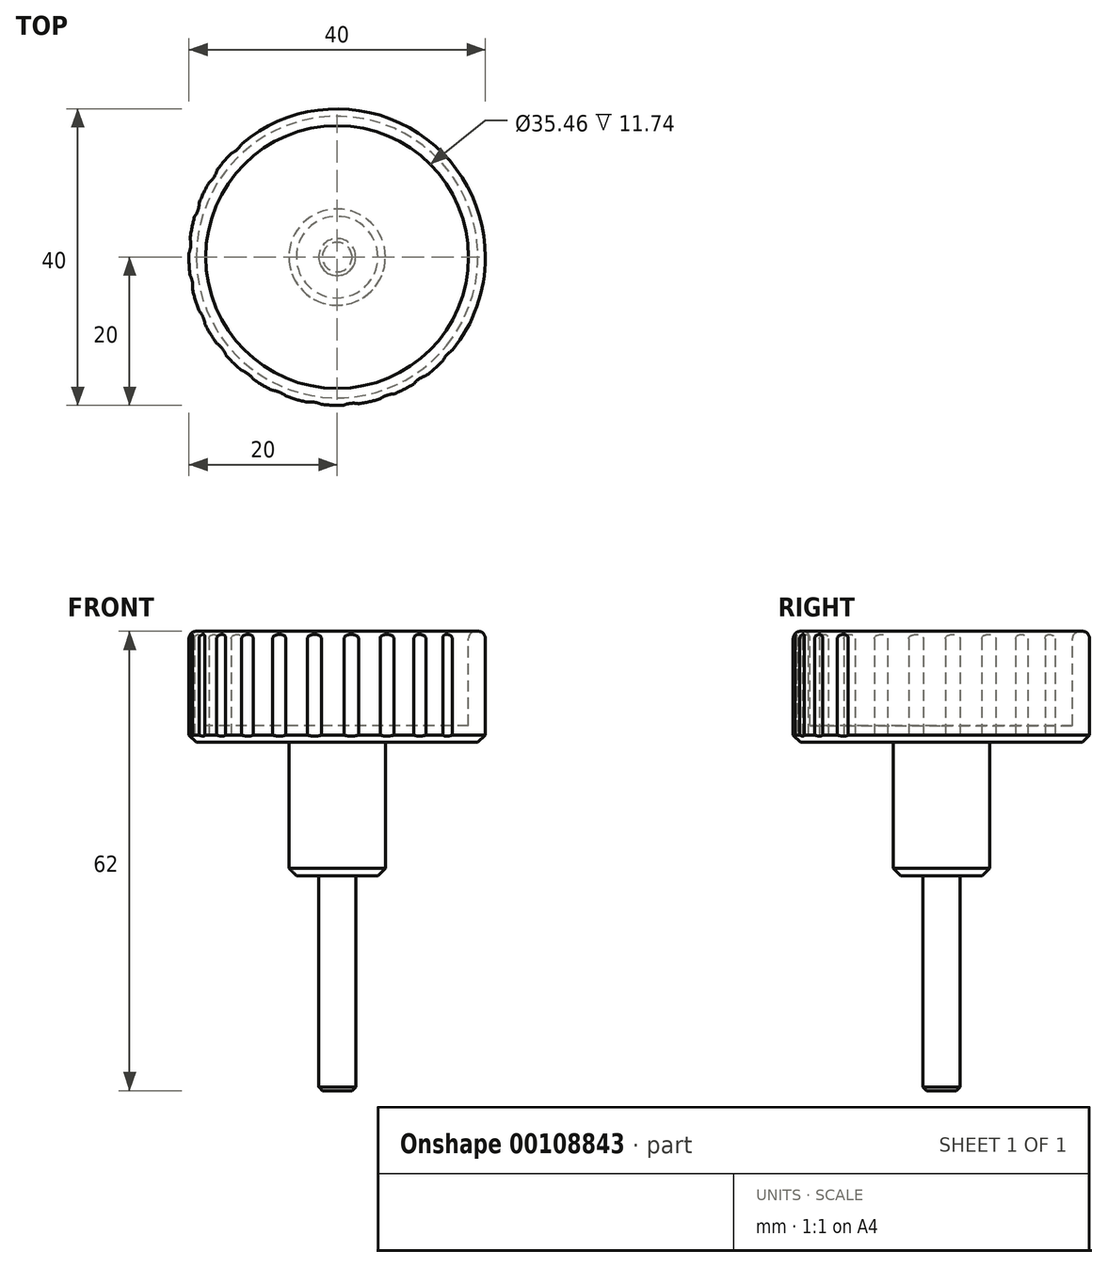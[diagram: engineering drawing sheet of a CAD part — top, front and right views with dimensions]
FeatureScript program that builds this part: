
annotation { "Feature Type Name" : "Feature", "Feature Type Description" : "" }
export const myFeature = defineFeature(function(context is Context, id is Id, definition is map)
    precondition{}
    {
        {
            var Q0;
            Q0=qCreatedBy(makeId("Front.planeOp"),FACE);
            var sketch = newSketch(context, id + "F0", { "sketchPlane" : qUnion([Q0])});
            skLineSegment(sketch, "E0", {"start": v(0, 56.29) * mm, "end": v(0, 50.52) * mm, "construction": true});
            skLineSegment(sketch, "E1", {"start": v(-48.57, 0) * mm, "end": v(48.76, 0) * mm, "construction": true});
            skLineSegment(sketch, "E2", {"start": v(-27.43, 50.52) * mm, "end": v(-17.73, 50.52) * mm, "construction": true});
            skLineSegment(sketch, "E3", {"start": v(-25.14, 35.52) * mm, "end": v(28.57, 35.52) * mm, "construction": true});
            skLineSegment(sketch, "E4", {"start": v(-11.83, 17.52) * mm, "end": v(17.7, 17.52) * mm, "construction": true});
            skLineSegment(sketch, "E5", {"start": v(-5.55, -11.48) * mm, "end": v(12.36, -11.48) * mm, "construction": true});
            skLineSegment(sketch, "E6", {"start": v(-17.73, 50.52) * mm, "end": v(-20, 50.52) * mm});
            skLineSegment(sketch, "E7", {"start": v(-20, 50.52) * mm, "end": v(-20, 35.52) * mm});
            skLineSegment(sketch, "E8", {"start": v(-20, 35.52) * mm, "end": v(-6.5, 35.52) * mm});
            skLineSegment(sketch, "E9", {"start": v(-6.5, 35.52) * mm, "end": v(-6.5, 17.52) * mm});
            skLineSegment(sketch, "E10", {"start": v(-6.5, 17.52) * mm, "end": v(-2.5, 17.52) * mm});
            skLineSegment(sketch, "E11", {"start": v(-2.5, 17.52) * mm, "end": v(-2.5, -11.48) * mm});
            skLineSegment(sketch, "E12", {"start": v(-2.5, -11.48) * mm, "end": v(0, -11.48) * mm});
            skLineSegment(sketch, "E13", {"start": v(0, -11.48) * mm, "end": v(0, 37.78) * mm});
            skLineSegment(sketch, "E14", {"start": v(-2.5, 17.52) * mm, "end": v(0, 17.52) * mm});
            skLineSegment(sketch, "E15", {"start": v(-17.73, 50.52) * mm, "end": v(-17.73, 37.78) * mm});
            skLineSegment(sketch, "E16", {"start": v(-17.73, 37.78) * mm, "end": v(0, 37.78) * mm});
            skLineSegment(sketch, "E17.trimOffspring", {"start": v(0, 50.52) * mm, "end": v(34.67, 50.52) * mm, "construction": true});
            skLineSegment(sketch, "E18.trimOffspring", {"start": v(0, 37.78) * mm, "end": v(0, -52.48) * mm, "construction": true});
            skSolve(sketch);
        }
        {
            var Q0;
            Q0=makeQuery(id+"F0.imprint","IMPRINT",FACE,{"disambiguationData":[TD([[makeQuery(id+"F0.imprint","IMPRINT",EDGE,{"derivedFrom":sQuery(id+"F0.wireOp",EDGE,"E11")}),1.0]])]});
            var Q1;
            Q1=sQuery(id+"F0.wireOp",EDGE,"E0");
            revolve(context, id + "F1", {"entities" : qUnion([Q0]), "axis" : qUnion([Q1]), "revolveType" : RevolveType.FULL});
        }
        {
            var Q0;
            Q0 = qSketchRegion(id + "F0", true);
            var Q1;
            Q1=sQuery(id+"F0.wireOp",EDGE,"E0");
            revolve(context, id + "F2", {"operationType" : NewBodyOperationType.ADD, "entities" : qUnion([Q0]), "axis" : qUnion([Q1]), "revolveType" : RevolveType.FULL});
        }
        {
            var Q0;
            Q0=makeQuery(id+"F2.opRevolve","SWEPT_EDGE",EDGE,{"disambiguationData":[OSD([sQuery(id+"F0.wireOp",EDGE,"E9"),sQuery(id+"F0.wireOp",EDGE,"E10")])]});
            var Q1;
            Q1=makeQuery(id+"F2.opRevolve","SWEPT_EDGE",EDGE,{"disambiguationData":[OSD([sQuery(id+"F0.wireOp",EDGE,"E7"),sQuery(id+"F0.wireOp",EDGE,"E8")])]});
            chamfer(context, id + "F3", {"entities" : qUnion([Q0, Q1]), "width" : 1 * mm, "tangentPropagation" : true});
        }
        {
            var Q0;
            Q0=makeQuery(id+"F1.opRevolve","SWEPT_EDGE",EDGE,{"disambiguationData":[OSD([sQuery(id+"F0.wireOp",EDGE,"E11"),sQuery(id+"F0.wireOp",EDGE,"E12")])]});
            chamfer(context, id + "F4", {"entities" : qUnion([Q0]), "width" : 0.5 * mm, "tangentPropagation" : true});
        }
        {
            var Q0;
            Q0=makeQuery(id+"F2.opRevolve","SWEPT_EDGE",EDGE,{"disambiguationData":[OSD([sQuery(id+"F0.wireOp",EDGE,"E6"),sQuery(id+"F0.wireOp",EDGE,"E7")])]});
            var Q1;
            Q1=makeQuery(id+"F2.opRevolve","SWEPT_EDGE",EDGE,{"disambiguationData":[OSD([sQuery(id+"F0.wireOp",EDGE,"E6"),sQuery(id+"F0.wireOp",EDGE,"E15")])]});
            fillet(context, id + "F5", {"entities" : qUnion([Q0, Q1]), "radius" : 1 * mm, "tangentPropagation" : true, "allowEdgeOverflow" : false});
        }
        {
            var Q0;
            Q0=makeQuery(id+"F2.opRevolve","SWEPT_FACE",FACE,{"disambiguationData":[OSD([sQuery(id+"F0.wireOp",EDGE,"E8")])]});
            cPlane(context, id + "F6", {"entities" : qUnion([Q0]), "cplaneType" : CPlaneType.OFFSET, "offset" : 0 * mm, "width" : 150 * mm, "height" : 150 * mm});
        }
        {
            var Q0;
            Q0=qCreatedBy(id+"F6.planeOp",FACE);
            var sketch = newSketch(context, id + "F7", { "sketchPlane" : qUnion([Q0])});
            skCircle(sketch, "E19", {"center": v(0, -23.03) * mm, "radius": 3.2 * mm});
            skCircle(sketch, "E20", {"center": v(0, 0) * mm, "radius": 23.02 * mm, "construction": true});
            skCircle(sketch, "E21.1.0", {"center": v(-5.67, -22.32) * mm, "radius": 3.2 * mm});
            skCircle(sketch, "E21.2.0", {"center": v(-11, -20.23) * mm, "radius": 3.2 * mm});
            skCircle(sketch, "E21.3.0", {"center": v(-15.65, -16.9) * mm, "radius": 3.2 * mm});
            skCircle(sketch, "E21.4.0", {"center": v(-19.33, -12.52) * mm, "radius": 3.2 * mm});
            skCircle(sketch, "E21.5.0", {"center": v(-21.82, -7.37) * mm, "radius": 3.2 * mm});
            skCircle(sketch, "E21.6.0", {"center": v(-22.96, -1.77) * mm, "radius": 3.2 * mm});
            skCircle(sketch, "E21.7.0", {"center": v(-22.69, 3.94) * mm, "radius": 3.2 * mm});
            skCircle(sketch, "E21.8.0", {"center": v(-21.02, 9.41) * mm, "radius": 3.2 * mm});
            skCircle(sketch, "E21.9.0", {"center": v(-18.05, 14.3) * mm, "radius": 3.2 * mm});
            skCircle(sketch, "E21.10.0", {"center": v(-13.97, 18.3) * mm, "radius": 3.2 * mm});
            skCircle(sketch, "E21.11.0", {"center": v(-9.03, 21.18) * mm, "radius": 3.2 * mm});
            skCircle(sketch, "E21.12.0", {"center": v(-3.53, 22.76) * mm, "radius": 3.2 * mm});
            skCircle(sketch, "E21.13.0", {"center": v(2.19, 22.92) * mm, "radius": 3.2 * mm});
            skCircle(sketch, "E21.14.0", {"center": v(7.77, 21.68) * mm, "radius": 3.2 * mm});
            skCircle(sketch, "E21.15.0", {"center": v(12.87, 19.1) * mm, "radius": 3.2 * mm});
            skCircle(sketch, "E21.16.0", {"center": v(17.18, 15.34) * mm, "radius": 3.2 * mm});
            skCircle(sketch, "E21.17.0", {"center": v(20.43, 10.63) * mm, "radius": 3.2 * mm});
            skCircle(sketch, "E21.18.0", {"center": v(22.42, 5.27) * mm, "radius": 3.2 * mm});
            skCircle(sketch, "E21.19.0", {"center": v(23.02, -0.42) * mm, "radius": 3.2 * mm});
            skCircle(sketch, "E21.20.0", {"center": v(22.21, -6.08) * mm, "radius": 3.2 * mm});
            skCircle(sketch, "E21.21.0", {"center": v(20.03, -11.36) * mm, "radius": 3.2 * mm});
            skCircle(sketch, "E21.22.0", {"center": v(16.61, -15.95) * mm, "radius": 3.2 * mm});
            skCircle(sketch, "E21.23.0", {"center": v(12.17, -19.55) * mm, "radius": 3.2 * mm});
            skCircle(sketch, "E21.24.0", {"center": v(6.98, -21.95) * mm, "radius": 3.2 * mm});
            skLineSegment(sketch, "E21.anchor1", {"start": v(0, 0) * mm, "end": v(0, -23.03) * mm, "construction": true});
            skLineSegment(sketch, "E21.anchor2", {"start": v(0, 0) * mm, "end": v(6.98, -21.95) * mm, "construction": true});
            skSolve(sketch);
        }
        {
            var Q0;
            {var subQ0=sQuery(id+"F7.wireOp",EDGE,"E21.2.0");var subQ1=sQuery(id+"F7.wireOp",EDGE,"E21.1.0");var subQ2=makeQuery(id+"F7.imprint","INTERSECT",VERTEX,{"disambiguationData":[OD(0.0)],"derivedFrom":[subQ1,subQ0]});Q0=makeQuery(id+"F7.imprint","IMPRINT",FACE,{"disambiguationData":[TD([[makeQuery(id+"F7.imprint","IMPRINT",EDGE,{"disambiguationData":[TD([[subQ2,-1.0]])],"derivedFrom":subQ1}),-1.0]])]});}
            var Q1;
            {var subQ0=sQuery(id+"F7.wireOp",EDGE,"E21.1.0");var subQ1=sQuery(id+"F7.wireOp",EDGE,"E19");var subQ2=makeQuery(id+"F7.imprint","INTERSECT",VERTEX,{"disambiguationData":[OD(0.0)],"derivedFrom":[subQ1,subQ0]});Q1=makeQuery(id+"F7.imprint","IMPRINT",FACE,{"disambiguationData":[TD([[makeQuery(id+"F7.imprint","IMPRINT",EDGE,{"disambiguationData":[TD([[subQ2,-1.0]])],"derivedFrom":subQ1}),-1.0]])]});}
            var Q2;
            {var subQ0=sQuery(id+"F7.wireOp",EDGE,"E21.1.0");var subQ1=sQuery(id+"F7.wireOp",EDGE,"E19");var subQ2=makeQuery(id+"F7.imprint","INTERSECT",VERTEX,{"disambiguationData":[OD(0.0)],"derivedFrom":[subQ1,subQ0]});Q2=makeQuery(id+"F7.imprint","IMPRINT",FACE,{"disambiguationData":[TD([[makeQuery(id+"F7.imprint","IMPRINT",EDGE,{"disambiguationData":[TD([[subQ2,1.0]])],"derivedFrom":subQ1}),1.0]])]});}
            var Q3;
            {var subQ0=sQuery(id+"F7.wireOp",EDGE,"E21.24.0");var subQ1=sQuery(id+"F7.wireOp",EDGE,"E21.23.0");var subQ2=makeQuery(id+"F7.imprint","INTERSECT",VERTEX,{"disambiguationData":[OD(0.0)],"derivedFrom":[subQ1,subQ0]});Q3=makeQuery(id+"F7.imprint","IMPRINT",FACE,{"disambiguationData":[TD([[makeQuery(id+"F7.imprint","IMPRINT",EDGE,{"disambiguationData":[TD([[subQ2,-1.0]])],"derivedFrom":subQ1}),-1.0]])]});}
            var Q4;
            {var subQ0=sQuery(id+"F7.wireOp",EDGE,"E21.23.0");var subQ1=sQuery(id+"F7.wireOp",EDGE,"E21.22.0");var subQ2=makeQuery(id+"F7.imprint","INTERSECT",VERTEX,{"disambiguationData":[OD(0.0)],"derivedFrom":[subQ1,subQ0]});Q4=makeQuery(id+"F7.imprint","IMPRINT",FACE,{"disambiguationData":[TD([[makeQuery(id+"F7.imprint","IMPRINT",EDGE,{"disambiguationData":[TD([[subQ2,-1.0]])],"derivedFrom":subQ1}),-1.0]])]});}
            var Q5;
            {var subQ0=sQuery(id+"F7.wireOp",EDGE,"E21.22.0");var subQ1=sQuery(id+"F7.wireOp",EDGE,"E21.21.0");var subQ2=makeQuery(id+"F7.imprint","INTERSECT",VERTEX,{"disambiguationData":[OD(0.0)],"derivedFrom":[subQ1,subQ0]});Q5=makeQuery(id+"F7.imprint","IMPRINT",FACE,{"disambiguationData":[TD([[makeQuery(id+"F7.imprint","IMPRINT",EDGE,{"disambiguationData":[TD([[subQ2,-1.0]])],"derivedFrom":subQ1}),-1.0]])]});}
            var Q6;
            {var subQ0=sQuery(id+"F7.wireOp",EDGE,"E21.21.0");var subQ1=sQuery(id+"F7.wireOp",EDGE,"E21.20.0");var subQ2=makeQuery(id+"F7.imprint","INTERSECT",VERTEX,{"disambiguationData":[OD(0.0)],"derivedFrom":[subQ1,subQ0]});Q6=makeQuery(id+"F7.imprint","IMPRINT",FACE,{"disambiguationData":[TD([[makeQuery(id+"F7.imprint","IMPRINT",EDGE,{"disambiguationData":[TD([[subQ2,-1.0]])],"derivedFrom":subQ1}),-1.0]])]});}
            var Q7;
            {var subQ0=sQuery(id+"F7.wireOp",EDGE,"E21.20.0");var subQ1=sQuery(id+"F7.wireOp",EDGE,"E21.19.0");var subQ2=makeQuery(id+"F7.imprint","INTERSECT",VERTEX,{"disambiguationData":[OD(0.0)],"derivedFrom":[subQ1,subQ0]});Q7=makeQuery(id+"F7.imprint","IMPRINT",FACE,{"disambiguationData":[TD([[makeQuery(id+"F7.imprint","IMPRINT",EDGE,{"disambiguationData":[TD([[subQ2,-1.0]])],"derivedFrom":subQ1}),-1.0]])]});}
            var Q8;
            {var subQ0=sQuery(id+"F7.wireOp",EDGE,"E21.19.0");var subQ1=sQuery(id+"F7.wireOp",EDGE,"E21.18.0");var subQ2=makeQuery(id+"F7.imprint","INTERSECT",VERTEX,{"disambiguationData":[OD(0.0)],"derivedFrom":[subQ1,subQ0]});Q8=makeQuery(id+"F7.imprint","IMPRINT",FACE,{"disambiguationData":[TD([[makeQuery(id+"F7.imprint","IMPRINT",EDGE,{"disambiguationData":[TD([[subQ2,-1.0]])],"derivedFrom":subQ1}),-1.0]])]});}
            var Q9;
            {var subQ0=sQuery(id+"F7.wireOp",EDGE,"E21.18.0");var subQ1=sQuery(id+"F7.wireOp",EDGE,"E21.17.0");var subQ2=makeQuery(id+"F7.imprint","INTERSECT",VERTEX,{"disambiguationData":[OD(0.0)],"derivedFrom":[subQ1,subQ0]});Q9=makeQuery(id+"F7.imprint","IMPRINT",FACE,{"disambiguationData":[TD([[makeQuery(id+"F7.imprint","IMPRINT",EDGE,{"disambiguationData":[TD([[subQ2,-1.0]])],"derivedFrom":subQ1}),-1.0]])]});}
            var Q10;
            {var subQ0=sQuery(id+"F7.wireOp",EDGE,"E21.17.0");var subQ1=sQuery(id+"F7.wireOp",EDGE,"E21.16.0");var subQ2=makeQuery(id+"F7.imprint","INTERSECT",VERTEX,{"disambiguationData":[OD(0.0)],"derivedFrom":[subQ1,subQ0]});Q10=makeQuery(id+"F7.imprint","IMPRINT",FACE,{"disambiguationData":[TD([[makeQuery(id+"F7.imprint","IMPRINT",EDGE,{"disambiguationData":[TD([[subQ2,-1.0]])],"derivedFrom":subQ1}),-1.0]])]});}
            var Q11;
            {var subQ0=sQuery(id+"F7.wireOp",EDGE,"E21.16.0");var subQ1=sQuery(id+"F7.wireOp",EDGE,"E21.15.0");var subQ2=makeQuery(id+"F7.imprint","INTERSECT",VERTEX,{"disambiguationData":[OD(0.0)],"derivedFrom":[subQ1,subQ0]});Q11=makeQuery(id+"F7.imprint","IMPRINT",FACE,{"disambiguationData":[TD([[makeQuery(id+"F7.imprint","IMPRINT",EDGE,{"disambiguationData":[TD([[subQ2,-1.0]])],"derivedFrom":subQ1}),-1.0]])]});}
            var Q12;
            {var subQ0=sQuery(id+"F7.wireOp",EDGE,"E21.15.0");var subQ1=sQuery(id+"F7.wireOp",EDGE,"E21.14.0");var subQ2=makeQuery(id+"F7.imprint","INTERSECT",VERTEX,{"disambiguationData":[OD(0.0)],"derivedFrom":[subQ1,subQ0]});Q12=makeQuery(id+"F7.imprint","IMPRINT",FACE,{"disambiguationData":[TD([[makeQuery(id+"F7.imprint","IMPRINT",EDGE,{"disambiguationData":[TD([[subQ2,-1.0]])],"derivedFrom":subQ1}),-1.0]])]});}
            var Q13;
            {var subQ0=sQuery(id+"F7.wireOp",EDGE,"E21.14.0");var subQ1=sQuery(id+"F7.wireOp",EDGE,"E21.13.0");var subQ2=makeQuery(id+"F7.imprint","INTERSECT",VERTEX,{"disambiguationData":[OD(0.0)],"derivedFrom":[subQ1,subQ0]});Q13=makeQuery(id+"F7.imprint","IMPRINT",FACE,{"disambiguationData":[TD([[makeQuery(id+"F7.imprint","IMPRINT",EDGE,{"disambiguationData":[TD([[subQ2,-1.0]])],"derivedFrom":subQ1}),-1.0]])]});}
            var Q14;
            {var subQ0=sQuery(id+"F7.wireOp",EDGE,"E21.13.0");var subQ1=sQuery(id+"F7.wireOp",EDGE,"E21.12.0");var subQ2=makeQuery(id+"F7.imprint","INTERSECT",VERTEX,{"disambiguationData":[OD(0.0)],"derivedFrom":[subQ1,subQ0]});Q14=makeQuery(id+"F7.imprint","IMPRINT",FACE,{"disambiguationData":[TD([[makeQuery(id+"F7.imprint","IMPRINT",EDGE,{"disambiguationData":[TD([[subQ2,-1.0]])],"derivedFrom":subQ1}),-1.0]])]});}
            var Q15;
            {var subQ0=sQuery(id+"F7.wireOp",EDGE,"E21.12.0");var subQ1=sQuery(id+"F7.wireOp",EDGE,"E21.11.0");var subQ2=makeQuery(id+"F7.imprint","INTERSECT",VERTEX,{"disambiguationData":[OD(0.0)],"derivedFrom":[subQ1,subQ0]});Q15=makeQuery(id+"F7.imprint","IMPRINT",FACE,{"disambiguationData":[TD([[makeQuery(id+"F7.imprint","IMPRINT",EDGE,{"disambiguationData":[TD([[subQ2,-1.0]])],"derivedFrom":subQ1}),-1.0]])]});}
            var Q16;
            {var subQ0=sQuery(id+"F7.wireOp",EDGE,"E21.10.0");var subQ1=sQuery(id+"F7.wireOp",EDGE,"E21.9.0");var subQ2=makeQuery(id+"F7.imprint","INTERSECT",VERTEX,{"disambiguationData":[OD(0.0)],"derivedFrom":[subQ1,subQ0]});Q16=makeQuery(id+"F7.imprint","IMPRINT",FACE,{"disambiguationData":[TD([[makeQuery(id+"F7.imprint","IMPRINT",EDGE,{"disambiguationData":[TD([[subQ2,-1.0]])],"derivedFrom":subQ1}),-1.0]])]});}
            var Q17;
            {var subQ0=sQuery(id+"F7.wireOp",EDGE,"E21.7.0");var subQ1=sQuery(id+"F7.wireOp",EDGE,"E21.6.0");var subQ2=makeQuery(id+"F7.imprint","INTERSECT",VERTEX,{"disambiguationData":[OD(0.0)],"derivedFrom":[subQ1,subQ0]});Q17=makeQuery(id+"F7.imprint","IMPRINT",FACE,{"disambiguationData":[TD([[makeQuery(id+"F7.imprint","IMPRINT",EDGE,{"disambiguationData":[TD([[subQ2,-1.0]])],"derivedFrom":subQ1}),-1.0]])]});}
            var Q18;
            {var subQ0=sQuery(id+"F7.wireOp",EDGE,"E21.6.0");var subQ1=sQuery(id+"F7.wireOp",EDGE,"E21.5.0");var subQ2=makeQuery(id+"F7.imprint","INTERSECT",VERTEX,{"disambiguationData":[OD(0.0)],"derivedFrom":[subQ1,subQ0]});Q18=makeQuery(id+"F7.imprint","IMPRINT",FACE,{"disambiguationData":[TD([[makeQuery(id+"F7.imprint","IMPRINT",EDGE,{"disambiguationData":[TD([[subQ2,-1.0]])],"derivedFrom":subQ1}),-1.0]])]});}
            var Q19;
            {var subQ0=sQuery(id+"F7.wireOp",EDGE,"E21.5.0");var subQ1=sQuery(id+"F7.wireOp",EDGE,"E21.4.0");var subQ2=makeQuery(id+"F7.imprint","INTERSECT",VERTEX,{"disambiguationData":[OD(0.0)],"derivedFrom":[subQ1,subQ0]});Q19=makeQuery(id+"F7.imprint","IMPRINT",FACE,{"disambiguationData":[TD([[makeQuery(id+"F7.imprint","IMPRINT",EDGE,{"disambiguationData":[TD([[subQ2,-1.0]])],"derivedFrom":subQ1}),-1.0]])]});}
            var Q20;
            {var subQ0=sQuery(id+"F7.wireOp",EDGE,"E21.4.0");var subQ1=sQuery(id+"F7.wireOp",EDGE,"E21.3.0");var subQ2=makeQuery(id+"F7.imprint","INTERSECT",VERTEX,{"disambiguationData":[OD(0.0)],"derivedFrom":[subQ1,subQ0]});Q20=makeQuery(id+"F7.imprint","IMPRINT",FACE,{"disambiguationData":[TD([[makeQuery(id+"F7.imprint","IMPRINT",EDGE,{"disambiguationData":[TD([[subQ2,-1.0]])],"derivedFrom":subQ1}),-1.0]])]});}
            var Q21;
            {var subQ0=sQuery(id+"F7.wireOp",EDGE,"E21.3.0");var subQ1=sQuery(id+"F7.wireOp",EDGE,"E21.2.0");var subQ2=makeQuery(id+"F7.imprint","INTERSECT",VERTEX,{"disambiguationData":[OD(0.0)],"derivedFrom":[subQ1,subQ0]});Q21=makeQuery(id+"F7.imprint","IMPRINT",FACE,{"disambiguationData":[TD([[makeQuery(id+"F7.imprint","IMPRINT",EDGE,{"disambiguationData":[TD([[subQ2,-1.0]])],"derivedFrom":subQ1}),-1.0]])]});}
            var Q22;
            {var subQ0=sQuery(id+"F7.wireOp",EDGE,"E21.11.0");var subQ1=sQuery(id+"F7.wireOp",EDGE,"E21.10.0");var subQ2=makeQuery(id+"F7.imprint","INTERSECT",VERTEX,{"disambiguationData":[OD(0.0)],"derivedFrom":[subQ1,subQ0]});Q22=makeQuery(id+"F7.imprint","IMPRINT",FACE,{"disambiguationData":[TD([[makeQuery(id+"F7.imprint","IMPRINT",EDGE,{"disambiguationData":[TD([[subQ2,-1.0]])],"derivedFrom":subQ1}),-1.0]])]});}
            var Q23;
            {var subQ0=sQuery(id+"F7.wireOp",EDGE,"E21.9.0");var subQ1=sQuery(id+"F7.wireOp",EDGE,"E21.8.0");var subQ2=makeQuery(id+"F7.imprint","INTERSECT",VERTEX,{"disambiguationData":[OD(0.0)],"derivedFrom":[subQ1,subQ0]});Q23=makeQuery(id+"F7.imprint","IMPRINT",FACE,{"disambiguationData":[TD([[makeQuery(id+"F7.imprint","IMPRINT",EDGE,{"disambiguationData":[TD([[subQ2,-1.0]])],"derivedFrom":subQ1}),-1.0]])]});}
            var Q24;
            {var subQ0=sQuery(id+"F7.wireOp",EDGE,"E21.8.0");var subQ1=sQuery(id+"F7.wireOp",EDGE,"E21.7.0");var subQ2=makeQuery(id+"F7.imprint","INTERSECT",VERTEX,{"disambiguationData":[OD(0.0)],"derivedFrom":[subQ1,subQ0]});Q24=makeQuery(id+"F7.imprint","IMPRINT",FACE,{"disambiguationData":[TD([[makeQuery(id+"F7.imprint","IMPRINT",EDGE,{"disambiguationData":[TD([[subQ2,-1.0]])],"derivedFrom":subQ1}),-1.0]])]});}
            extrude(context, id + "F8", {"entities" : qUnion([Q0, Q1, Q2, Q3, Q4, Q5, Q6, Q7, Q8, Q9, Q10, Q11, Q12, Q13, Q14, Q15, Q16, Q17, Q18, Q19, Q20, Q21, Q22, Q23, Q24]), "operationType" : NewBodyOperationType.REMOVE, "oppositeDirection" : true, "depth" : 25 * mm});
        }
    });
